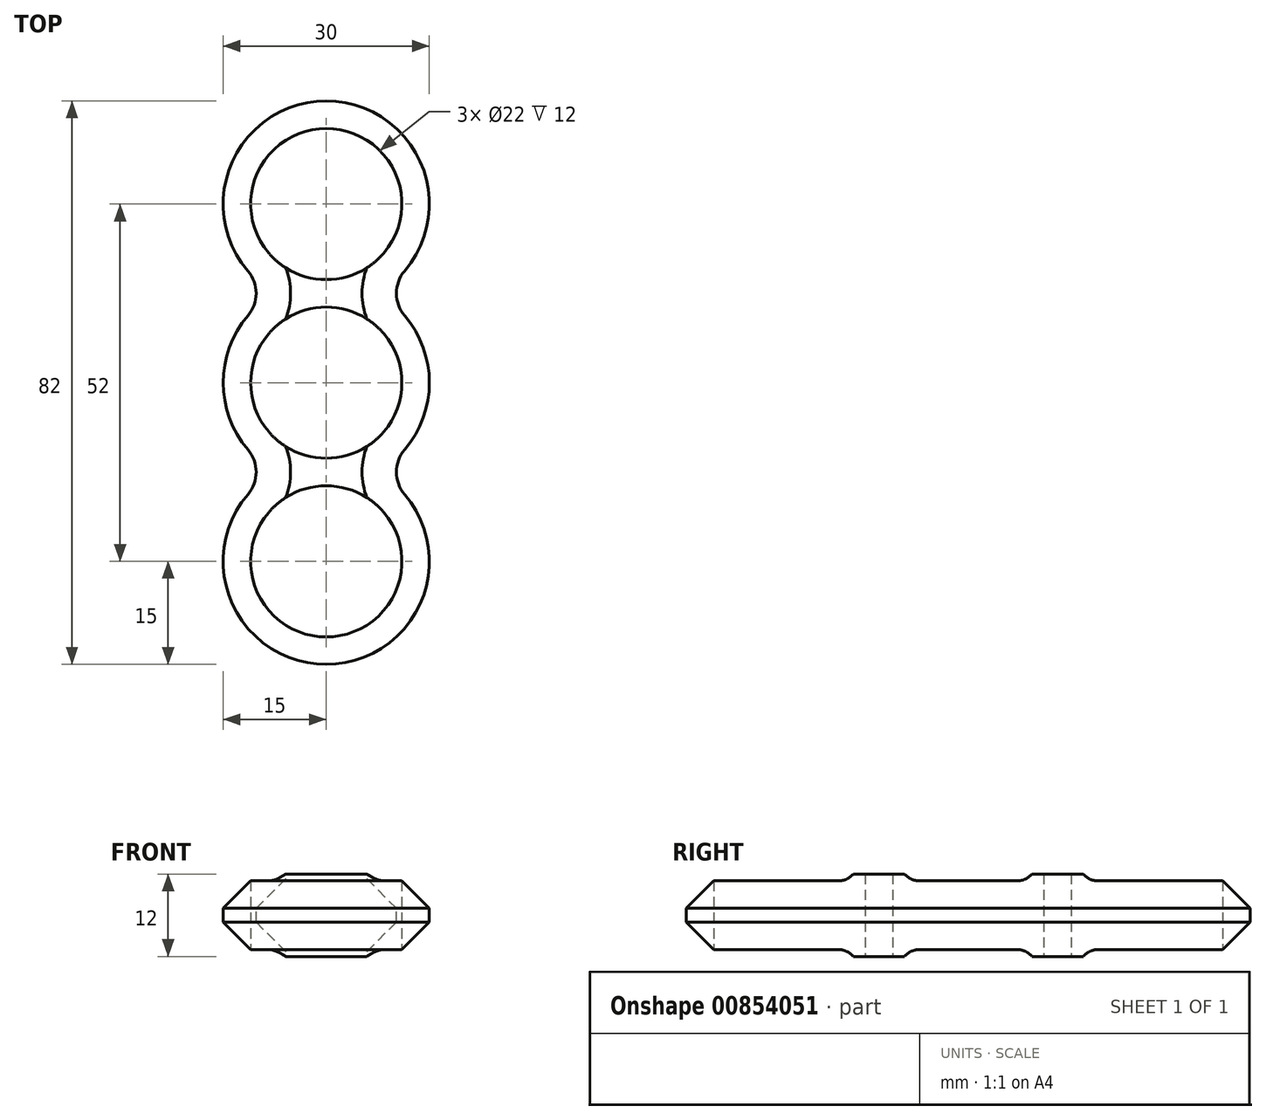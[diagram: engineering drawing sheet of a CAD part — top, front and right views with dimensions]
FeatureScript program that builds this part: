
annotation { "Feature Type Name" : "Feature", "Feature Type Description" : "" }
export const myFeature = defineFeature(function(context is Context, id is Id, definition is map)
    precondition{}
    {
        {
            var Q0;
            Q0=qCreatedBy(makeId("Top.planeOp"),FACE);
            var sketch = newSketch(context, id + "F0", { "sketchPlane" : qUnion([Q0])});
            skCircle(sketch, "E0", {"center": v(0, 0) * mm, "radius": 11 * mm});
            skCircle(sketch, "E1", {"center": v(0, 26) * mm, "radius": 11 * mm});
            skCircle(sketch, "E2", {"center": v(0, -26) * mm, "radius": 11 * mm});
            skCircle(sketch, "E3", {"center": v(0, 0) * mm, "radius": 15 * mm});
            skArc(sketch, "E4", {"start": v(0, 11) * mm, "mid": v(3.87, 40.5) * mm, "end": v(-7.48, 13) * mm});
            skCircle(sketch, "E5", {"center": v(0, -26) * mm, "radius": 15 * mm});
            skPoint(sketch, "E6", {"position": v(7.48, 13) * mm});
            skPoint(sketch, "E7", {"position": v(7.48, -13) * mm});
            skPoint(sketch, "E8", {"position": v(-7.48, -13) * mm});
            skSolve(sketch);
        }
        {
            var Q0;
            Q0 = qSketchRegion(id + "F0", true);
            extrude(context, id + "F1", {"entities" : qUnion([Q0]), "depth" : 12 * mm, "offsetDistance" : 25 * mm});
        }
        {
            var Q0;
            {var subQ0=sQuery(id+"F0.wireOp",EDGE,"E4");var subQ1=sQuery(id+"F0.wireOp",EDGE,"E3");Q0=makeQuery(id+"F1.opExtrude","SWEPT_EDGE",EDGE,{"disambiguationData":[OSD([subQ1,subQ0]),TDD([makeQuery(id+"F0.imprint","INTERSECT",VERTEX,{"disambiguationData":[OD(0.0)],"derivedFrom":[subQ1,subQ0]})])]});}
            var Q1;
            {var subQ0=sQuery(id+"F0.wireOp",EDGE,"E5");var subQ1=sQuery(id+"F0.wireOp",EDGE,"E3");Q1=makeQuery(id+"F1.opExtrude","SWEPT_EDGE",EDGE,{"disambiguationData":[OSD([subQ1,subQ0]),TDD([makeQuery(id+"F0.imprint","INTERSECT",VERTEX,{"disambiguationData":[OD(1.0)],"derivedFrom":[subQ1,subQ0]})])]});}
            var Q2;
            {var subQ0=sQuery(id+"F0.wireOp",EDGE,"E5");var subQ1=sQuery(id+"F0.wireOp",EDGE,"E3");Q2=makeQuery(id+"F1.opExtrude","SWEPT_EDGE",EDGE,{"disambiguationData":[OSD([subQ1,subQ0]),TDD([makeQuery(id+"F0.imprint","INTERSECT",VERTEX,{"disambiguationData":[OD(0.0)],"derivedFrom":[subQ1,subQ0]})])]});}
            var Q3;
            {var subQ0=sQuery(id+"F0.wireOp",EDGE,"E4");var subQ1=sQuery(id+"F0.wireOp",EDGE,"E3");Q3=makeQuery(id+"F1.opExtrude","SWEPT_EDGE",EDGE,{"disambiguationData":[OSD([subQ1,subQ0]),TDD([makeQuery(id+"F0.imprint","INTERSECT",VERTEX,{"disambiguationData":[OD(1.0)],"derivedFrom":[subQ1,subQ0]})])]});}
            fillet(context, id + "F2", {"entities" : qUnion([Q0, Q1, Q2, Q3]), "radius" : 5 * mm, "tangentPropagation" : true, "allowEdgeOverflow" : false});
        }
        {
            var Q0;
            Q0=makeQuery(id+"F1.opExtrude","CAP_EDGE",EDGE,{"disambiguationData":[OSD([sQuery(id+"F0.wireOp",EDGE,"E4")])],"isStart":false});
            var Q1;
            Q1=makeQuery(id+"F1.opExtrude","CAP_EDGE",EDGE,{"disambiguationData":[OSD([sQuery(id+"F0.wireOp",EDGE,"E4")])],"isStart":true});
            chamfer(context, id + "F3", {"entities" : qUnion([Q0, Q1]), "width" : 5 * mm, "tangentPropagation" : true});
        }
    });
